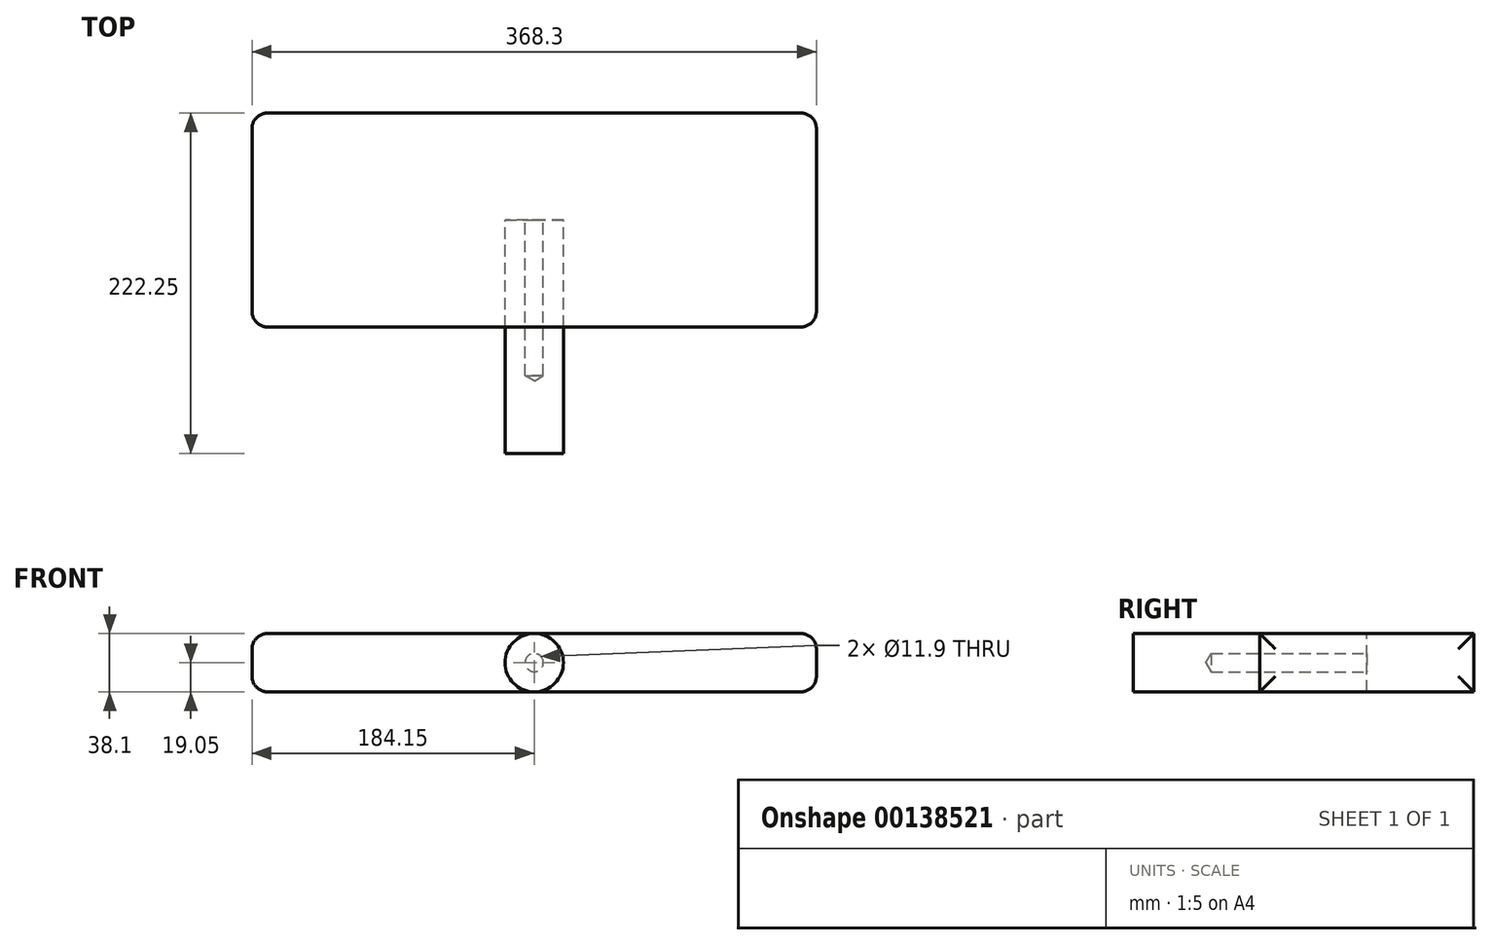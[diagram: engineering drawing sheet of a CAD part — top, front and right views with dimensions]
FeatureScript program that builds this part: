
annotation { "Feature Type Name" : "Feature", "Feature Type Description" : "" }
export const myFeature = defineFeature(function(context is Context, id is Id, definition is map)
    precondition{}
    {
        {
            var Q0;
            Q0=qCreatedBy(makeId("Front.planeOp"),FACE);
            var sketch = newSketch(context, id + "F0", { "sketchPlane" : qUnion([Q0])});
            skCircle(sketch, "E0", {"center": v(0, 0) * mm, "radius": 19.05 * mm});
            skSolve(sketch);
        }
        {
            var Q0;
            Q0 = qSketchRegion(id + "F0", true);
            var Q1;
            Q1=makeQuery(id+"F0.imprint","IMPRINT",FACE,{"disambiguationData":[TD([[makeQuery(id+"F0.imprint","IMPRINT",EDGE,{"derivedFrom":sQuery(id+"F0.wireOp",EDGE,"E0")}),1.0]])]});
            extrude(context, id + "F1", {"entities" : qUnion([Q0, Q1]), "depth" : 152.4 * mm});
        }
        {
            var Q0;
            Q0=sQuery(id+"F0.wireOp",VERTEX,"E0.center");
            var Q1;
            Q1=makeQuery(id+"F1.opExtrude","SWEPT_BODY",BODY,{"disambiguationData":[OSD([sQuery(id+"F0.wireOp",EDGE,"E0")])]});
            hole(context, id + "F2", {"style" : HoleStyle.SIMPLE, "endStyle" : HoleEndStyle.BLIND, "oppositeDirection" : true, "standardTappedOrClearance" : lookupTablePath({ "standard" : "ANSI", "fit" : "Normal (ASME)", "size" : "7/16", "type" : "Clearance" }), "standardBlindInLast" : lookupTablePath({ "fit" : "Free", "standard" : "ANSI", "size" : "7/16", "type" : "Clearance" }), "holeDiameter" : 11.9 * mm, "holeDepth" : 101.6 * mm, "locations" : qUnion([Q0]), "scope" : qUnion([Q1])});
        }
        {
            var Q0;
            Q0=qCreatedBy(makeId("Top.planeOp"),FACE);
            var sketch = newSketch(context, id + "F3", { "sketchPlane" : qUnion([Q0])});
            skLineSegment(sketch, "E1.bottom", {"start": v(184.15, 69.85) * mm, "end": v(-184.15, 69.85) * mm});
            skLineSegment(sketch, "E1.top", {"start": v(184.15, -69.85) * mm, "end": v(-184.15, -69.85) * mm});
            skLineSegment(sketch, "E1.left", {"start": v(184.15, 69.85) * mm, "end": v(184.15, -69.85) * mm});
            skLineSegment(sketch, "E1.right", {"start": v(-184.15, 69.85) * mm, "end": v(-184.15, -69.85) * mm});
            skPoint(sketch, "E1.middle", {"position": v(0, 0) * mm});
            skPoint(sketch, "E2", {"position": v(-133.35, 0) * mm});
            skPoint(sketch, "E3", {"position": v(133.35, 0) * mm});
            skPoint(sketch, "E4", {"position": v(133.35, 38.1) * mm});
            skPoint(sketch, "E5", {"position": v(133.35, -38.1) * mm});
            skPoint(sketch, "E6", {"position": v(-133.35, 38.1) * mm});
            skPoint(sketch, "E7", {"position": v(-133.35, -38.1) * mm});
            skPoint(sketch, "E8", {"position": v(-184.15, -38.1) * mm});
            skPoint(sketch, "E9", {"position": v(-184.15, 0) * mm});
            skPoint(sketch, "E10", {"position": v(-184.15, 38.1) * mm});
            skPoint(sketch, "E11", {"position": v(184.15, 38.1) * mm});
            skPoint(sketch, "E12", {"position": v(184.15, 0) * mm});
            skPoint(sketch, "E13", {"position": v(184.15, -38.1) * mm});
            skSolve(sketch);
        }
        {
            var Q0;
            Q0=makeQuery(id+"F3.imprint","IMPRINT",FACE,{"disambiguationData":[TD([[makeQuery(id+"F3.imprint","IMPRINT",EDGE,{"derivedFrom":sQuery(id+"F3.wireOp",EDGE,"E1.bottom")}),1.0]])]});
            extrude(context, id + "F4", {"entities" : qUnion([Q0]), "endBound" : BoundingType.SYMMETRIC, "depth" : 38.1 * mm});
        }
        {
            var Q0;
            Q0=makeQuery(id+"F4.opExtrude","SWEPT_FACE",FACE,{"disambiguationData":[OSD([sQuery(id+"F3.wireOp",EDGE,"E1.right")])]});
            fillet(context, id + "F5", {"entities" : qUnion([Q0]), "radius" : 10.16 * mm, "tangentPropagation" : true, "allowEdgeOverflow" : false});
        }
        {
            var Q0;
            Q0=makeQuery(id+"F4.opExtrude","SWEPT_FACE",FACE,{"disambiguationData":[OSD([sQuery(id+"F3.wireOp",EDGE,"E1.left")])]});
            fillet(context, id + "F6", {"entities" : qUnion([Q0]), "radius" : 10.16 * mm, "tangentPropagation" : true, "allowEdgeOverflow" : false});
        }
    });
